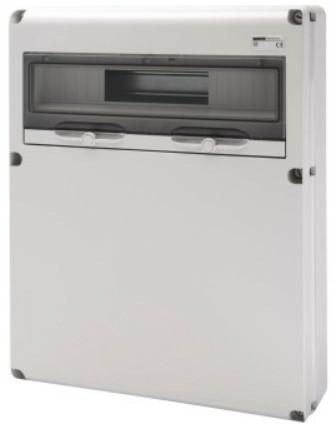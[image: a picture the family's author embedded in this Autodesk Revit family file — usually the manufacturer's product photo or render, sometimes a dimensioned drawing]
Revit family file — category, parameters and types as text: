
# Revit family: Building-QuadriIEC309-GEWISS-68QDIN-QUADRI-20MOD_CIECO
name_source: partatom
category: Apparecchi elettrici
units: mm (PartAtom-declared; Revit-internal decimal feet)

## family parameters
Condiviso = No
Host = Superficie
Mantenere orientamento annotazione = Sì
Punto di calcolo locali = Sì
Quota connettore circolare = Usa diametro
Taglio con vuoti quando caricato = No
Tipo di parte = Normale

## types (1)
- GW68012N - Q-DIN 20M COP.CIECO 560x450x135 IP65
    Catalogo = BUILDING
    Catalogo Serie = 68 QDIN
    Classe isolamento = II
    Codice EAN = 8011564744820
    Codice Electrocod = 2242
    Colore = Grigio RAL 7035
    Conformità normativa = EN 60208 - EN 60670-1 - IEC 60670-24
    Descrizione = Q-DIN 20M COP.CIECO 560x450x135 IP65
    Glow Wire Test = 650°C
    Grado di protezione = IP65
    IDF = ebf329cc-5afa-41a6-a7ec-8eb83a2ae5aa
    IDT = 91d94f96-0e3b-43d6-a2ed-d5af9a5ddb7e
    Immagine tipo = GW68012N.jpg
    L_Moduli = 380 mm  [stored 1.24672 ft]
    Modello = GW68012N
    N. coperchi ciechi in dotazione = -
    N. mod. EN 50022 = 20
    N. prese alloggiabili = Coperchio cieco
    N_Moduli = 20 mm  [stored 0.0656168 ft]
    POMELLO = bianco
    PRESA = rosso
    Potenza dissipabile A (W) = 30
    Potenza dissipabile B (W) = 92
    Produttore = GEWISS S.p.A.
    Prospetto di default = 1219 mm
    Resistenza agli urti = IK09
    SEO = Quadretto
    STRUTTURA = RAL - 7035
    STRUTTURA ALTA = Poche
    Scheda Tecnica = https://www.gewiss.com
    Spostamento_S = 1000 mm  [stored 3.28084 ft]
    Temperatura di utilizzo = -25 +40 °C
    Termopressione con biglia = 70 °C
    Tipo versione = Vuoto
    Tipologia di installazione = Da parete
    URL = https://www.gewiss.com
    VETRO = Vetro
    Versione file RFA = 21.5

note: [stored X ft] marks values corroborated as IEEE doubles in the binary element streams (Revit-internal decimal feet)

## geometry (parser evidence)
native form markers: Sweep x4
no freeform markers — native parametric forms only
